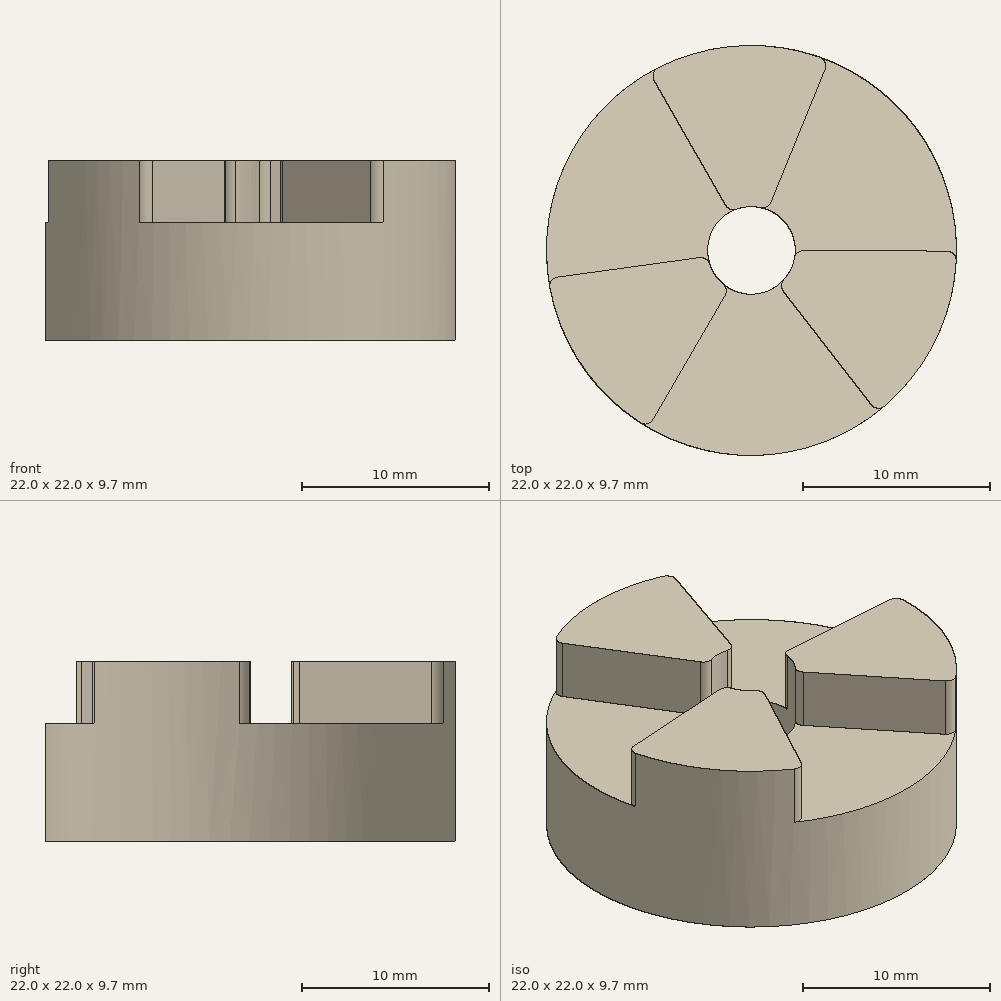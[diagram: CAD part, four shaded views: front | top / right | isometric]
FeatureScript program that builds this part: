
annotation { "Feature Type Name" : "Feature", "Feature Type Description" : "" }
export const myFeature = defineFeature(function(context is Context, id is Id, definition is map)
    precondition{}
    {
        {
            var Q0;
            Q0=qCreatedBy(makeId("Top.planeOp"),FACE);
            var sketch = newSketch(context, id + "F0", { "sketchPlane" : qUnion([Q0])});
            skCircle(sketch, "E0", {"center": v(0, 0) * mm, "radius": 11 * mm});
            skCircle(sketch, "E1", {"center": v(0, 0) * mm, "radius": 2.35 * mm});
            skLineSegment(sketch, "E2", {"start": v(0, 0) * mm, "end": v(4.15, 10.19) * mm});
            skLineSegment(sketch, "E3", {"start": v(0, 0) * mm, "end": v(-5.47, 9.54) * mm});
            skLineSegment(sketch, "E4.1.0", {"start": v(0, 0) * mm, "end": v(11, -0.03) * mm});
            skLineSegment(sketch, "E4.1.1", {"start": v(0, 0) * mm, "end": v(6.75, -8.69) * mm});
            skLineSegment(sketch, "E4.2.0", {"start": v(0, 0) * mm, "end": v(-5.53, -9.5) * mm});
            skLineSegment(sketch, "E4.2.1", {"start": v(0, 0) * mm, "end": v(-10.9, -1.5) * mm});
            skLineSegment(sketch, "E4.anchor1", {"start": v(0, 0) * mm, "end": v(-5.47, 9.54) * mm, "construction": true});
            skLineSegment(sketch, "E4.anchor2", {"start": v(0, 0) * mm, "end": v(-5.53, -9.5) * mm, "construction": true});
            skSolve(sketch);
        }
        {
            var Q0;
            {var subQ0=sQuery(id+"F0.wireOp",EDGE,"E2");var subQ1=sQuery(id+"F0.wireOp",EDGE,"E0");var subQ2=makeQuery(id+"F0.imprint","INTERSECT",VERTEX,{"derivedFrom":[subQ1,subQ0]});Q0=makeQuery(id+"F0.imprint","IMPRINT",FACE,{"disambiguationData":[TD([[makeQuery(id+"F0.imprint","IMPRINT",EDGE,{"disambiguationData":[TD([[subQ2,-1.0]])],"derivedFrom":subQ1}),1.0]])]});}
            var Q1;
            {var subQ0=sQuery(id+"F0.wireOp",EDGE,"E4.2.0");var subQ1=sQuery(id+"F0.wireOp",EDGE,"E0");var subQ2=makeQuery(id+"F0.imprint","INTERSECT",VERTEX,{"derivedFrom":[subQ1,subQ0]});Q1=makeQuery(id+"F0.imprint","IMPRINT",FACE,{"disambiguationData":[TD([[makeQuery(id+"F0.imprint","IMPRINT",EDGE,{"disambiguationData":[TD([[subQ2,1.0]])],"derivedFrom":subQ1}),1.0]])]});}
            var Q2;
            {var subQ0=sQuery(id+"F0.wireOp",EDGE,"E4.1.0");var subQ1=sQuery(id+"F0.wireOp",EDGE,"E0");var subQ2=makeQuery(id+"F0.imprint","INTERSECT",VERTEX,{"derivedFrom":[subQ1,subQ0]});Q2=makeQuery(id+"F0.imprint","IMPRINT",FACE,{"disambiguationData":[TD([[makeQuery(id+"F0.imprint","IMPRINT",EDGE,{"disambiguationData":[TD([[subQ2,1.0]])],"derivedFrom":subQ1}),1.0]])]});}
            extrude(context, id + "F1", {"entities" : qUnion([Q0, Q1, Q2]), "depth" : 3.3 * mm});
        }
        {
            var Q0;
            {var subQ0=sQuery(id+"F0.wireOp",EDGE,"33BuIZ9v-IkX0-KjEr-VNsg-VApjckLjgjfI");var subQ1=sQuery(id+"F0.wireOp",EDGE,"E0");var subQ2=makeQuery(id+"F0.imprint","INTERSECT",VERTEX,{"derivedFrom":[subQ1,subQ0]});Q0=makeQuery(id+"F0.imprint","IMPRINT",FACE,{"disambiguationData":[TD([[makeQuery(id+"F0.imprint","IMPRINT",EDGE,{"disambiguationData":[TD([[subQ2,1.0]])],"derivedFrom":subQ1}),1.0]])]});}
            var Q1;
            {var subQ0=sQuery(id+"F0.wireOp",EDGE,"dZoegOkE-iBWH-g3UK-yCjy-q1fHpqfjE5M4");var subQ1=sQuery(id+"F0.wireOp",EDGE,"E0");var subQ2=makeQuery(id+"F0.imprint","INTERSECT",VERTEX,{"derivedFrom":[subQ1,subQ0]});Q1=makeQuery(id+"F0.imprint","IMPRINT",FACE,{"disambiguationData":[TD([[makeQuery(id+"F0.imprint","IMPRINT",EDGE,{"disambiguationData":[TD([[subQ2,1.0]])],"derivedFrom":subQ1}),1.0]])]});}
            var Q2;
            {var subQ0=sQuery(id+"F0.wireOp",EDGE,"073fcc1c-5e5f-4306-95f4-ba863140295b.1.1");var subQ1=sQuery(id+"F0.wireOp",EDGE,"E0");var subQ2=makeQuery(id+"F0.imprint","INTERSECT",VERTEX,{"derivedFrom":[subQ1,subQ0]});Q2=makeQuery(id+"F0.imprint","IMPRINT",FACE,{"disambiguationData":[TD([[makeQuery(id+"F0.imprint","IMPRINT",EDGE,{"disambiguationData":[TD([[subQ2,1.0]])],"derivedFrom":subQ1}),1.0]])]});}
            var Q3;
            {var subQ0=sQuery(id+"F0.wireOp",EDGE,"073fcc1c-5e5f-4306-95f4-ba863140295b.1.0");var subQ1=sQuery(id+"F0.wireOp",EDGE,"E0");var subQ2=makeQuery(id+"F0.imprint","INTERSECT",VERTEX,{"derivedFrom":[subQ1,subQ0]});Q3=makeQuery(id+"F0.imprint","IMPRINT",FACE,{"disambiguationData":[TD([[makeQuery(id+"F0.imprint","IMPRINT",EDGE,{"disambiguationData":[TD([[subQ2,1.0]])],"derivedFrom":subQ1}),1.0]])]});}
            var Q4;
            {var subQ0=sQuery(id+"F0.wireOp",EDGE,"073fcc1c-5e5f-4306-95f4-ba863140295b.2.0");var subQ1=sQuery(id+"F0.wireOp",EDGE,"E0");var subQ2=makeQuery(id+"F0.imprint","INTERSECT",VERTEX,{"derivedFrom":[subQ1,subQ0]});Q4=makeQuery(id+"F0.imprint","IMPRINT",FACE,{"disambiguationData":[TD([[makeQuery(id+"F0.imprint","IMPRINT",EDGE,{"disambiguationData":[TD([[subQ2,1.0]])],"derivedFrom":subQ1}),1.0]])]});}
            var Q5;
            {var subQ0=sQuery(id+"F0.wireOp",EDGE,"33BuIZ9v-IkX0-KjEr-VNsg-VApjckLjgjfI");var subQ1=sQuery(id+"F0.wireOp",EDGE,"E0");var subQ2=makeQuery(id+"F0.imprint","INTERSECT",VERTEX,{"derivedFrom":[subQ1,subQ0]});Q5=makeQuery(id+"F0.imprint","IMPRINT",FACE,{"disambiguationData":[TD([[makeQuery(id+"F0.imprint","IMPRINT",EDGE,{"disambiguationData":[TD([[subQ2,-1.0]])],"derivedFrom":subQ1}),1.0]])]});}
            extrude(context, id + "F2", {"entities" : qUnion([Q0, Q1, Q2, Q3, Q4, Q5]), "operationType" : NewBodyOperationType.ADD, "oppositeDirection" : true, "depth" : 6.35 * mm});
        }
        {
            var Q0;
            Q0=makeQuery(id+"F1.opExtrude","SWEPT_EDGE",EDGE,{"disambiguationData":[OSD([sQuery(id+"F0.wireOp",EDGE,"E0"),sQuery(id+"F0.wireOp",EDGE,"E2")])]});
            var Q1;
            Q1=makeQuery(id+"F1.opExtrude","SWEPT_EDGE",EDGE,{"disambiguationData":[OSD([sQuery(id+"F0.wireOp",EDGE,"E0"),sQuery(id+"F0.wireOp",EDGE,"E4.1.0")])]});
            var Q2;
            Q2=makeQuery(id+"F1.opExtrude","SWEPT_EDGE",EDGE,{"disambiguationData":[OSD([sQuery(id+"F0.wireOp",EDGE,"E0"),sQuery(id+"F0.wireOp",EDGE,"E3")])]});
            var Q3;
            Q3=makeQuery(id+"F1.opExtrude","SWEPT_EDGE",EDGE,{"disambiguationData":[OSD([sQuery(id+"F0.wireOp",EDGE,"E0"),sQuery(id+"F0.wireOp",EDGE,"E4.1.1")])]});
            var Q4;
            Q4=makeQuery(id+"F1.opExtrude","SWEPT_EDGE",EDGE,{"disambiguationData":[OSD([sQuery(id+"F0.wireOp",EDGE,"E0"),sQuery(id+"F0.wireOp",EDGE,"E4.2.0")])]});
            var Q5;
            Q5=makeQuery(id+"F1.opExtrude","SWEPT_EDGE",EDGE,{"disambiguationData":[OSD([sQuery(id+"F0.wireOp",EDGE,"E0"),sQuery(id+"F0.wireOp",EDGE,"E4.2.1")])]});
            fillet(context, id + "F3", {"entities" : qUnion([Q0, Q1, Q2, Q3, Q4, Q5]), "radius" : 0.5 * mm, "tangentPropagation" : true, "allowEdgeOverflow" : false});
        }
        {
            var Q0;
            Q0=makeQuery(id+"F1.opExtrude","SWEPT_EDGE",EDGE,{"disambiguationData":[OSD([sQuery(id+"F0.wireOp",EDGE,"E1"),sQuery(id+"F0.wireOp",EDGE,"E4.2.1")])]});
            var Q1;
            Q1=makeQuery(id+"F1.opExtrude","SWEPT_EDGE",EDGE,{"disambiguationData":[OSD([sQuery(id+"F0.wireOp",EDGE,"E1"),sQuery(id+"F0.wireOp",EDGE,"E4.2.0")])]});
            var Q2;
            Q2=makeQuery(id+"F1.opExtrude","SWEPT_EDGE",EDGE,{"disambiguationData":[OSD([sQuery(id+"F0.wireOp",EDGE,"E1"),sQuery(id+"F0.wireOp",EDGE,"E3")])]});
            var Q3;
            Q3=makeQuery(id+"F1.opExtrude","SWEPT_EDGE",EDGE,{"disambiguationData":[OSD([sQuery(id+"F0.wireOp",EDGE,"E1"),sQuery(id+"F0.wireOp",EDGE,"E2")])]});
            var Q4;
            Q4=makeQuery(id+"F1.opExtrude","SWEPT_EDGE",EDGE,{"disambiguationData":[OSD([sQuery(id+"F0.wireOp",EDGE,"E1"),sQuery(id+"F0.wireOp",EDGE,"E4.1.1")])]});
            var Q5;
            Q5=makeQuery(id+"F1.opExtrude","SWEPT_EDGE",EDGE,{"disambiguationData":[OSD([sQuery(id+"F0.wireOp",EDGE,"E1"),sQuery(id+"F0.wireOp",EDGE,"E4.1.0")])]});
            fillet(context, id + "F4", {"entities" : qUnion([Q0, Q1, Q2, Q3, Q4, Q5]), "radius" : 0.5 * mm, "tangentPropagation" : true, "allowEdgeOverflow" : false});
        }
    });
